# Revit family: NBS_HeatraeSadia_DrctHotWtrStrgCylndrs_MEGAFLOEcoPlus_300DDDD
name_source: partatom
category: Plumbing Fixtures
revit_build: Autodesk Revit 2014 (Build: 20130709_2115(x64)
units: mm (PartAtom-declared; Revit-internal decimal feet)

## types (1)
- 300DDDD
    AssetType = Fixed
    BIMObjectName = NBS_HeatraeSadia_DirectHotWaterStorageCylinders_MEGAFLOEcoPlus-300DDDD
    CW Connection = Yes
    Color = White
    Connections = 1” BSP male connections to fit 28 mm pipes
    ControlHousingMaterial = NBS_Concept
    CylinderMaterial = NBS_Concept
    Description = Unvented direct hot water cylinder
    DurationUnit = year
    EffectiveCapacity = 0 m³
    ElectricalDeviceNominalPower = 0
    ErPRating = C
    FirstCurvatureRadius = 0 mm  [stored 0 ft]
    Fixing = Floor fixed
    FlowRate = ≤130 L/min
    HW Connection = Yes
    HasProtectiveEarth = No
    HeatUpTime = 310 minutes
    Height = 2052 mm
    HotWaterSystemOutletHeight = 1681 mm  [stored 5.51509 ft]
    IfcExportAs = IfcTankType
    IfcExportType = STORAGE
    ImmersionHeater = Four 3 kW titanium elements with integral thermostat and thermal cut-out
    ManufacturerName = Heatrae Sadia
    ManufacturerURL = www.heatraesadia.com
    Material = Outer casing: Plastic-coated corrosion-proofed steel; Water container: Duplex stainless steel
    MaterialThickness = 0 mm  [stored 0 ft]
    ModelNumber = 950:50:701
    ModelReference = MEGAFLO Eco Plus - 300DDDD
    NBSCertification = http://www.nationalbimlibrary.com
    NBSDescription = Direct hot water storage cylinders
    NBSReference = 90-15-35/310
    Name = DirectHotWaterStorageCylinders_MEGAFLOEcoPlus-300DDDD_HeatraeSadia
    NominalCapacity = 8.5 m³
    NominalCurrent = 0
    NominalDepth = 1737 mm  [stored 5.69882 ft]
    NominalFrequencyRange = 50.0, 60.0
    NominalLengthOrDiameter = 579 mm
    NominalVoltage = 230.0, 240.0
    NominalWidthOrDiameter = 579 mm
    NumberOfPoles = 0
    OperatingWeight = 346
    OutletTemperatureRange = 15-60°C
    PatternType = Vertical cylinder
    PhaseAngle = 0.00°
    ProductInformation = www.heatraesadia.com/docs/Megaflo_Eco_Plus_Technical_Data.pdf
    SafetyFeatures = Manually resettable cut-out on each heating element operates at 85°C, temperature and pressure relief valve factory set to operate at 10 bar and 90°C
    SecondCurvatureRadius = 0 mm  [stored 0 ft]
    Shape = Cylinder
    Size = 2052 x 579 x 579 mm
    SupplyPressureRange = 1.5-16.0 bar
    TemperaturePressureReliefValveHeight = 1573 mm  [stored 5.16076 ft]
    ThermalInsulation = 60 mm thick CFC/HCFC free (ODP zero) polyurethane
    ThirdPartyCertification = Kiwa approved, Nemko approved
    Uniclass2 = 90-90-87/421
    Uniclass2015Description = Direct hot water storage cylinders
    Uniclass2015Reference = Pr_60_50_20_21
    Uniclass2015Version = Products v1.1
    UsageCurrent = 0
    ValveMaterial = NBS_Concept
    Vent Connection = No
    Version = 1
    WarrantyDurationParts = 2
    WarrantyDurationUnit = year
    WarrantyStartDate = 1900-12-31T23:59:59
    Waste Connection = No
    Width = 579 mm

note: [stored X ft] marks values corroborated as IEEE doubles in the binary element streams (Revit-internal decimal feet)

## geometry (parser evidence)
native form markers: Blend x3, Sweep x7
no freeform markers — native parametric forms only
